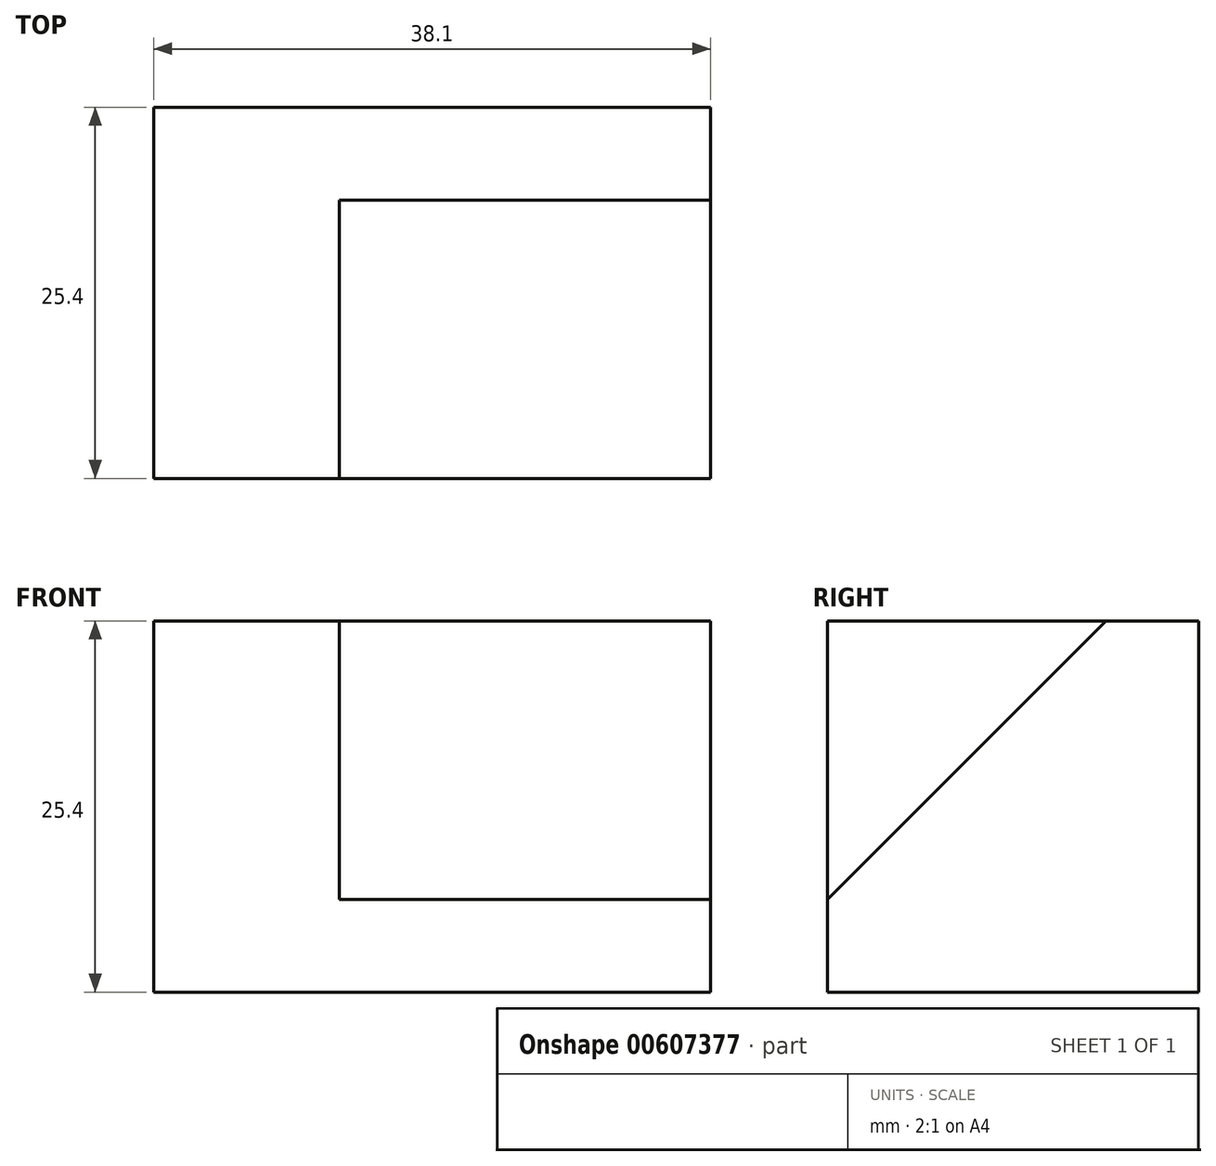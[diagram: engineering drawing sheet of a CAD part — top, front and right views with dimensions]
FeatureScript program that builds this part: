
annotation { "Feature Type Name" : "Feature", "Feature Type Description" : "" }
export const myFeature = defineFeature(function(context is Context, id is Id, definition is map)
    precondition{}
    {
        {
            var Q0;
            Q0=qCreatedBy(makeId("Top.planeOp"),FACE);
            var sketch = newSketch(context, id + "F0", { "sketchPlane" : qUnion([Q0])});
            skLineSegment(sketch, "E0", {"start": v(0, 0) * mm, "end": v(0, 25.4) * mm});
            skLineSegment(sketch, "E1", {"start": v(0, 25.4) * mm, "end": v(38.1, 25.4) * mm});
            skLineSegment(sketch, "E2", {"start": v(38.1, 25.4) * mm, "end": v(38.1, 0) * mm});
            skLineSegment(sketch, "E3", {"start": v(0, 0) * mm, "end": v(38.1, 0) * mm});
            skSolve(sketch);
        }
        {
            var Q0;
            Q0=makeQuery(id+"F0.imprint","IMPRINT",FACE,{"disambiguationData":[TD([[makeQuery(id+"F0.imprint","IMPRINT",EDGE,{"derivedFrom":sQuery(id+"F0.wireOp",EDGE,"E0")}),-1.0]])]});
            extrude(context, id + "F1", {"entities" : qUnion([Q0]), "depth" : 25.4 * mm, "offsetDistance" : 25.4 * mm});
        }
        {
            var Q0;
            Q0=makeQuery(id+"F1.opExtrude","SWEPT_FACE",FACE,{"disambiguationData":[OSD([sQuery(id+"F0.wireOp",EDGE,"E2")])]});
            var sketch = newSketch(context, id + "F2", { "sketchPlane" : qUnion([Q0])});
            skLineSegment(sketch, "E4", {"start": v(25.4, 25.4) * mm, "end": v(19.05, 25.4) * mm});
            skLineSegment(sketch, "E5", {"start": v(0, 0) * mm, "end": v(0, 6.35) * mm});
            skLineSegment(sketch, "E6", {"start": v(0, 6.35) * mm, "end": v(19.05, 25.4) * mm});
            skSolve(sketch);
        }
        {
            var Q0;
            Q0 = qSketchRegion(id + "F2", true);
            var Q1;
            {var subQ0=sQuery(id+"F2.wireOp",EDGE,"E6");Q1=makeQuery(id+"F2.imprint","IMPRINT",FACE,{"disambiguationData":[TD([[makeQuery(id+"F2.imprint","IMPRINT",EDGE,{"derivedFrom":subQ0}),1.0]])]});}
            extrude(context, id + "F3", {"entities" : qUnion([Q0, Q1]), "operationType" : NewBodyOperationType.REMOVE, "oppositeDirection" : true, "depth" : 25.4 * mm, "offsetDistance" : 25.4 * mm});
        }
    });
